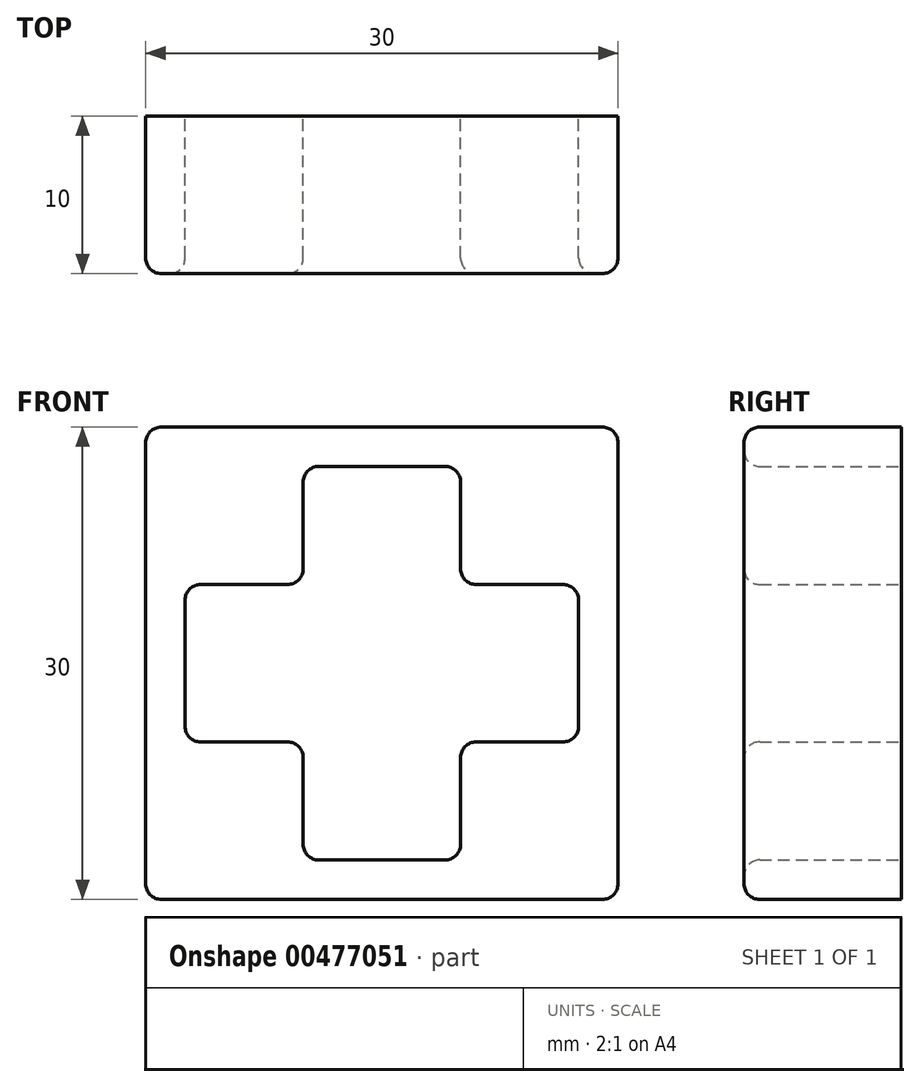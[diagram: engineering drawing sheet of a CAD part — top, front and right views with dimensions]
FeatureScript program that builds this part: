
annotation { "Feature Type Name" : "Feature", "Feature Type Description" : "" }
export const myFeature = defineFeature(function(context is Context, id is Id, definition is map)
    precondition{}
    {
        {
            var Q0;
            Q0=qCreatedBy(makeId("Front.planeOp"),FACE);
            var sketch = newSketch(context, id + "F0", { "sketchPlane" : qUnion([Q0])});
            skLineSegment(sketch, "E0.bottom", {"start": v(-5, -12.5) * mm, "end": v(5, -12.5) * mm});
            skLineSegment(sketch, "E0.top", {"start": v(-5, 12.5) * mm, "end": v(5, 12.5) * mm});
            skLineSegment(sketch, "E0.left", {"start": v(-5, -12.5) * mm, "end": v(-5, 12.5) * mm});
            skLineSegment(sketch, "E0.right", {"start": v(5, -12.5) * mm, "end": v(5, 12.5) * mm});
            skPoint(sketch, "E0.middle", {"position": v(0, 0) * mm});
            skLineSegment(sketch, "E1.bottom", {"start": v(-7.5, -15) * mm, "end": v(7.5, -15) * mm});
            skLineSegment(sketch, "E1.top", {"start": v(-7.5, 15) * mm, "end": v(7.5, 15) * mm});
            skLineSegment(sketch, "E1.left", {"start": v(-7.5, -15) * mm, "end": v(-7.5, 15) * mm});
            skLineSegment(sketch, "E1.right", {"start": v(7.5, -15) * mm, "end": v(7.5, 15) * mm});
            skLineSegment(sketch, "E2.bottom", {"start": v(-12.5, -5) * mm, "end": v(12.5, -5) * mm});
            skLineSegment(sketch, "E2.top", {"start": v(-12.5, 5) * mm, "end": v(12.5, 5) * mm});
            skLineSegment(sketch, "E2.left", {"start": v(-12.5, -5) * mm, "end": v(-12.5, 5) * mm});
            skLineSegment(sketch, "E2.right", {"start": v(12.5, -5) * mm, "end": v(12.5, 5) * mm});
            skLineSegment(sketch, "E3.bottom", {"start": v(-15, -7.5) * mm, "end": v(15, -7.5) * mm});
            skLineSegment(sketch, "E3.top", {"start": v(-15, 7.5) * mm, "end": v(15, 7.5) * mm});
            skLineSegment(sketch, "E3.left", {"start": v(-15, -7.5) * mm, "end": v(-15, 7.5) * mm});
            skLineSegment(sketch, "E3.right", {"start": v(15, -7.5) * mm, "end": v(15, 7.5) * mm});
            skLineSegment(sketch, "E4.bottom", {"start": v(-15, -15) * mm, "end": v(15, -15) * mm});
            skLineSegment(sketch, "E4.top", {"start": v(-15, 15) * mm, "end": v(15, 15) * mm});
            skLineSegment(sketch, "E4.left", {"start": v(-15, -15) * mm, "end": v(-15, 15) * mm});
            skLineSegment(sketch, "E4.right", {"start": v(15, -15) * mm, "end": v(15, 15) * mm});
            skSolve(sketch);
        }
        {
            var Q0;
            Q0 = qSketchRegion(id + "F0", true);
            var Q1;
            {var subQ0=sQuery(id+"F0.wireOp",EDGE,"E2.top");var subQ1=sQuery(id+"F0.wireOp",EDGE,"E0.left");var subQ2=makeQuery(id+"F0.imprint","INTERSECT",VERTEX,{"derivedFrom":[subQ1,subQ0]});Q1=makeQuery(id+"F0.imprint","IMPRINT",FACE,{"disambiguationData":[TD([[makeQuery(id+"F0.imprint","IMPRINT",EDGE,{"disambiguationData":[TD([[subQ2,-1.0]])],"derivedFrom":subQ1}),1.0]])]});}
            var Q2;
            {var subQ0=sQuery(id+"F0.wireOp",EDGE,"E2.top");var subQ1=sQuery(id+"F0.wireOp",EDGE,"E0.right");var subQ2=makeQuery(id+"F0.imprint","INTERSECT",VERTEX,{"derivedFrom":[subQ1,subQ0]});Q2=makeQuery(id+"F0.imprint","IMPRINT",FACE,{"disambiguationData":[TD([[makeQuery(id+"F0.imprint","IMPRINT",EDGE,{"disambiguationData":[TD([[subQ2,-1.0]])],"derivedFrom":subQ1}),-1.0]])]});}
            var Q3;
            {var subQ0=sQuery(id+"F0.wireOp",EDGE,"E3.bottom");var subQ1=sQuery(id+"F0.wireOp",EDGE,"E0.right");var subQ2=makeQuery(id+"F0.imprint","INTERSECT",VERTEX,{"derivedFrom":[subQ1,subQ0]});Q3=makeQuery(id+"F0.imprint","IMPRINT",FACE,{"disambiguationData":[TD([[makeQuery(id+"F0.imprint","IMPRINT",EDGE,{"disambiguationData":[TD([[subQ2,-1.0]])],"derivedFrom":subQ1}),-1.0]])]});}
            var Q4;
            {var subQ0=sQuery(id+"F0.wireOp",EDGE,"E3.bottom");var subQ1=sQuery(id+"F0.wireOp",EDGE,"E0.left");var subQ2=makeQuery(id+"F0.imprint","INTERSECT",VERTEX,{"derivedFrom":[subQ1,subQ0]});Q4=makeQuery(id+"F0.imprint","IMPRINT",FACE,{"disambiguationData":[TD([[makeQuery(id+"F0.imprint","IMPRINT",EDGE,{"disambiguationData":[TD([[subQ2,-1.0]])],"derivedFrom":subQ1}),1.0]])]});}
            extrude(context, id + "F1", {"entities" : qUnion([Q0, Q1, Q2, Q3, Q4]), "depth" : 10 * mm});
        }
        {
            var Q0;
            Q0=makeQuery(id+"F1.opExtrude","SWEPT_EDGE",EDGE,{"disambiguationData":[OSD([sQuery(id+"F0.wireOp",EDGE,"E0.left"),sQuery(id+"F0.wireOp",EDGE,"E2.top")])]});
            var Q1;
            Q1=makeQuery(id+"F1.opExtrude","SWEPT_EDGE",EDGE,{"disambiguationData":[OSD([sQuery(id+"F0.wireOp",EDGE,"E0.top"),sQuery(id+"F0.wireOp",EDGE,"E0.left")])]});
            var Q2;
            Q2=makeQuery(id+"F1.opExtrude","SWEPT_EDGE",EDGE,{"disambiguationData":[OSD([sQuery(id+"F0.wireOp",EDGE,"E2.top"),sQuery(id+"F0.wireOp",EDGE,"E2.left")])]});
            var Q3;
            Q3=makeQuery(id+"F1.opExtrude","SWEPT_EDGE",EDGE,{"disambiguationData":[OSD([sQuery(id+"F0.wireOp",EDGE,"E0.top"),sQuery(id+"F0.wireOp",EDGE,"E0.right")])]});
            var Q4;
            Q4=makeQuery(id+"F1.opExtrude","SWEPT_EDGE",EDGE,{"disambiguationData":[OSD([sQuery(id+"F0.wireOp",EDGE,"E0.right"),sQuery(id+"F0.wireOp",EDGE,"E2.top")])]});
            var Q5;
            Q5=makeQuery(id+"F1.opExtrude","SWEPT_EDGE",EDGE,{"disambiguationData":[OSD([sQuery(id+"F0.wireOp",EDGE,"E2.top"),sQuery(id+"F0.wireOp",EDGE,"E2.right")])]});
            var Q6;
            Q6=makeQuery(id+"F1.opExtrude","SWEPT_EDGE",EDGE,{"disambiguationData":[OSD([sQuery(id+"F0.wireOp",EDGE,"E2.bottom"),sQuery(id+"F0.wireOp",EDGE,"E2.right")])]});
            var Q7;
            Q7=makeQuery(id+"F1.opExtrude","SWEPT_EDGE",EDGE,{"disambiguationData":[OSD([sQuery(id+"F0.wireOp",EDGE,"E0.right"),sQuery(id+"F0.wireOp",EDGE,"E2.bottom")])]});
            var Q8;
            Q8=makeQuery(id+"F1.opExtrude","SWEPT_EDGE",EDGE,{"disambiguationData":[OSD([sQuery(id+"F0.wireOp",EDGE,"E0.bottom"),sQuery(id+"F0.wireOp",EDGE,"E0.right")])]});
            var Q9;
            Q9=makeQuery(id+"F1.opExtrude","SWEPT_EDGE",EDGE,{"disambiguationData":[OSD([sQuery(id+"F0.wireOp",EDGE,"E0.bottom"),sQuery(id+"F0.wireOp",EDGE,"E0.left")])]});
            var Q10;
            Q10=makeQuery(id+"F1.opExtrude","SWEPT_EDGE",EDGE,{"disambiguationData":[OSD([sQuery(id+"F0.wireOp",EDGE,"E0.left"),sQuery(id+"F0.wireOp",EDGE,"E2.bottom")])]});
            var Q11;
            Q11=makeQuery(id+"F1.opExtrude","SWEPT_EDGE",EDGE,{"disambiguationData":[OSD([sQuery(id+"F0.wireOp",EDGE,"E2.bottom"),sQuery(id+"F0.wireOp",EDGE,"E2.left")])]});
            fillet(context, id + "F2", {"entities" : qUnion([Q0, Q1, Q2, Q3, Q4, Q5, Q6, Q7, Q8, Q9, Q10, Q11]), "radius" : 1 * mm, "tangentPropagation" : true, "allowEdgeOverflow" : false});
        }
        {
            var Q0;
            Q0=makeQuery(id+"F1.opExtrude","CAP_EDGE",EDGE,{"disambiguationData":[OSD([sQuery(id+"F0.wireOp",EDGE,"E4.right")])],"isStart":false});
            var Q1;
            Q1=makeQuery(id+"F1.opExtrude","CAP_EDGE",EDGE,{"disambiguationData":[OSD([sQuery(id+"F0.wireOp",EDGE,"E4.top")])],"isStart":false});
            var Q2;
            Q2=makeQuery(id+"F1.opExtrude","CAP_EDGE",EDGE,{"disambiguationData":[OSD([sQuery(id+"F0.wireOp",EDGE,"E4.left")])],"isStart":false});
            var Q3;
            Q3=makeQuery(id+"F1.opExtrude","CAP_EDGE",EDGE,{"disambiguationData":[OSD([sQuery(id+"F0.wireOp",EDGE,"E4.bottom")])],"isStart":false});
            var Q4;
            {var subQ0=sQuery(id+"F0.wireOp",EDGE,"E2.bottom");Q4=makeQuery(id+"F1.opExtrude","CAP_EDGE",EDGE,{"disambiguationData":[OSD([subQ0]),TDD([makeQuery(id+"F0.imprint","IMPRINT",EDGE,{"disambiguationData":[TD([[makeQuery(id+"F0.imprint","INTERSECT",VERTEX,{"derivedFrom":[subQ0,sQuery(id+"F0.wireOp",EDGE,"E2.left")]}),-1.0]])],"derivedFrom":subQ0}),makeQuery(id+"F0.imprint","IMPRINT",EDGE,{"disambiguationData":[TD([[makeQuery(id+"F0.imprint","INTERSECT",VERTEX,{"derivedFrom":[sQuery(id+"F0.wireOp",EDGE,"E0.left"),subQ0]}),1.0]])],"derivedFrom":subQ0})])],"isStart":false});}
            var Q5;
            Q5=makeQuery(id+"F1.opExtrude","SWEPT_EDGE",EDGE,{"disambiguationData":[OSD([sQuery(id+"F0.wireOp",EDGE,"E4.bottom"),sQuery(id+"F0.wireOp",EDGE,"E4.left")])]});
            var Q6;
            Q6=makeQuery(id+"F1.opExtrude","SWEPT_EDGE",EDGE,{"disambiguationData":[OSD([sQuery(id+"F0.wireOp",EDGE,"E4.bottom"),sQuery(id+"F0.wireOp",EDGE,"E4.right")])]});
            var Q7;
            Q7=makeQuery(id+"F1.opExtrude","SWEPT_EDGE",EDGE,{"disambiguationData":[OSD([sQuery(id+"F0.wireOp",EDGE,"E4.top"),sQuery(id+"F0.wireOp",EDGE,"E4.right")])]});
            var Q8;
            Q8=makeQuery(id+"F1.opExtrude","SWEPT_EDGE",EDGE,{"disambiguationData":[OSD([sQuery(id+"F0.wireOp",EDGE,"E4.top"),sQuery(id+"F0.wireOp",EDGE,"E4.left")])]});
            fillet(context, id + "F3", {"entities" : qUnion([Q0, Q1, Q2, Q3, Q4, Q5, Q6, Q7, Q8]), "radius" : 1 * mm, "tangentPropagation" : true, "allowEdgeOverflow" : false});
        }
    });
